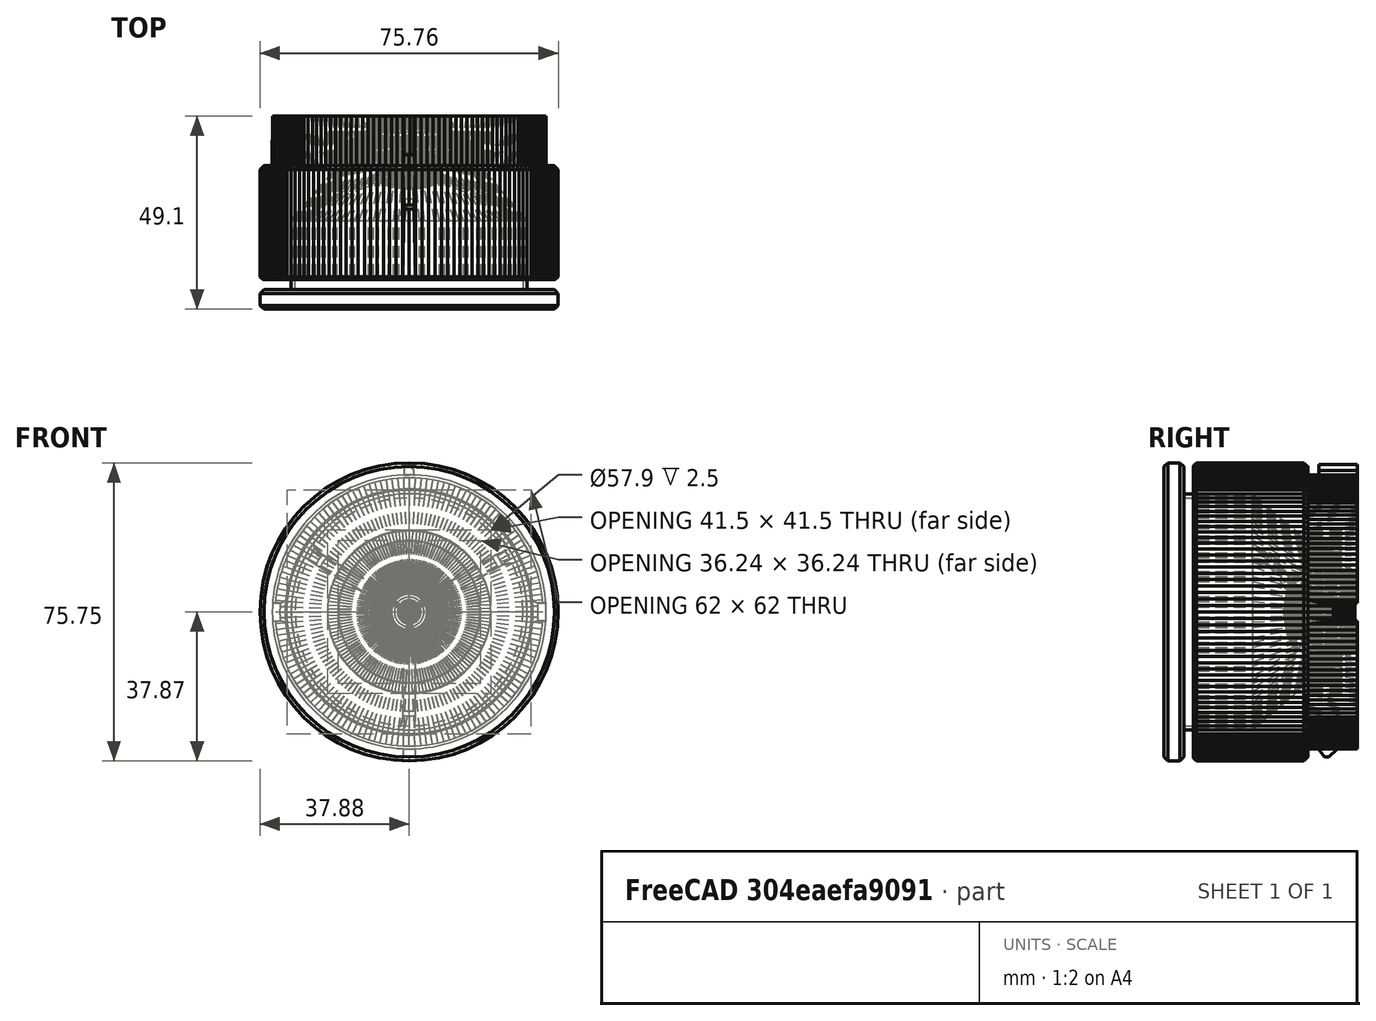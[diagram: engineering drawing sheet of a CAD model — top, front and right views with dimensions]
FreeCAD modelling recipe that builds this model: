
FCSTD DOCUMENT  (FreeCAD 1.1R20260325 (Git shallow))
Label: Hopper_Fix
License: All rights reserved
LicenseURL: https://en.wikipedia.org/wiki/All_rights_reserved
objects: App::Point×3, Sketcher::SketchObject×3, Part::Feature×2, PartDesign::Body×2, PartDesign::Pad×2, Mesh::Feature×1, Part::Refine×1, PartDesign::FeatureBase×1, PartDesign::Chamfer×1, App::Part×1
note: 22 computed .brp shape members not serialized (recipe doc carries the construction recipe); baked Part::Feature solids carry a one-line shape summary decoded from their .brp

FEATURE [Mesh::Feature] hopper_v4_with_insert
FEATURE [Part::Feature] hopper_v4_with_insert001
  shape: bbox 75.63 x 41.6 x 75.63 mm, 10708 faces, 0 solids (baked)
FEATURE [Part::Feature] hopper_v4_with_insert001_solid  label="hopper_v4_with_insert001 (Solid)"
  shape: bbox 75.63 x 41.6 x 75.63 mm, 10708 faces (baked)
FEATURE [Part::Refine] hopper_v4_with_insert001_solid001  label="hopper_v4_with_insert001 (Solid)001"
  Source = -> hopper_v4_with_insert001_solid
FEATURE [App::Point] Origin001
  Role = Origin
FEATURE [PartDesign::FeatureBase] BaseFeature
  BaseFeature = -> hopper_v4_with_insert001_solid001
  Suppressed = false
FEATURE [Sketcher::SketchObject] Sketch
  ArcFitTolerance = 1e-06
  AttachmentSupport = -> [BaseFeature]
  ExternalTypes = [0]
  FullyConstrained = true
  MakeInternals = false
  MapMode = 5
  Placement = pos=(0,-29,0) rot=(1,0,0;1.5708rad)
  _ExternalGeoVersion = 1
FEATURE [PartDesign::Body] Body
  AllowCompound = true
  BaseFeature = -> hopper_v4_with_insert001_solid001
  Group = -> [BaseFeature,Sketch]
  Origin = -> Origin
  Tip = -> BaseFeature
FEATURE [Sketcher::SketchObject] Sketch001
  ArcFitTolerance = 1e-06
  AttachmentSupport = -> [BaseFeature]
  ExternalTypes = [0]
  FullyConstrained = true
  MakeInternals = false
  MapMode = 5
  Placement = pos=(0,-29,0) rot=(1,0,0;1.5708rad)
  _ExternalGeoVersion = 1
  sketch-geometry (2):
    g0: Circle CenterX=0 CenterY=0 CenterZ=0 NormalX=0 NormalY=0 NormalZ=1 AngleXU=0 Radius=29.95
    g1: Circle CenterX=0 CenterY=0 CenterZ=0 NormalX=0 NormalY=0 NormalZ=1 AngleXU=0 Radius=28.95
  constraints (4):
    c: Coincident(g0,g-1)
    c: Diameter(g0) = 59.9
    c: Diameter(g1) = 57.9
    c: Coincident(g1,g0)
FEATURE [App::Point] Origin003
  Role = Origin
FEATURE [App::Point] Origin005  label="Origin006"
  Role = Origin
FEATURE [PartDesign::Pad] Pad
  Direction = (0,-1,0)
  Length = 2.5
  Length2 = 10
  Profile = -> Sketch001
  ReferenceAxis = -> Sketch001 [N_Axis]
  Refine = true
  SideType = 0
  Suppressed = false
  Type = 0
  Type2 = 0
FEATURE [Sketcher::SketchObject] Sketch002
  ArcFitTolerance = 1e-06
  AttachmentSupport = -> [Pad]
  ExternalTypes = [0]
  FullyConstrained = true
  MakeInternals = false
  MapMode = 5
  Placement = pos=(0,-31.5,8.8e-15) rot=(1,0,0;1.5708rad)
  _ExternalGeoVersion = 1
  sketch-geometry (1):
    g0: Circle CenterX=0 CenterY=0 CenterZ=0 NormalX=0 NormalY=0 NormalZ=1 AngleXU=0 Radius=37.875
  constraints (2):
    c: Diameter(g0) = 75.75
    c: Coincident(g0,g-1)
FEATURE [PartDesign::Pad] Pad001
  BaseFeature = -> Pad
  Direction = (0,-1,0)
  Length = 5
  Length2 = 10
  Profile = -> Sketch002
  ReferenceAxis = -> Sketch002 [N_Axis]
  Refine = true
  SideType = 0
  Suppressed = false
  Type = 0
  Type2 = 0
FEATURE [PartDesign::Chamfer] Chamfer
  Angle = 45
  Base = -> Pad001 [Edge5,Edge9]
  BaseFeature = -> Pad001
  ChamferType = 0
  FlipDirection = false
  Refine = true
  Size = 1
  Size2 = 1
  SupportTransform = false
  Suppressed = false
  UseAllEdges = false
FEATURE [PartDesign::Body] Body001
  AllowCompound = true
  Group = -> [Sketch001,Pad,Sketch002,Pad001,Chamfer]
  Origin = -> Origin004
  Tip = -> Chamfer
FEATURE [App::Part] Part
  Group = -> [Body001]
  Origin = -> Origin002
